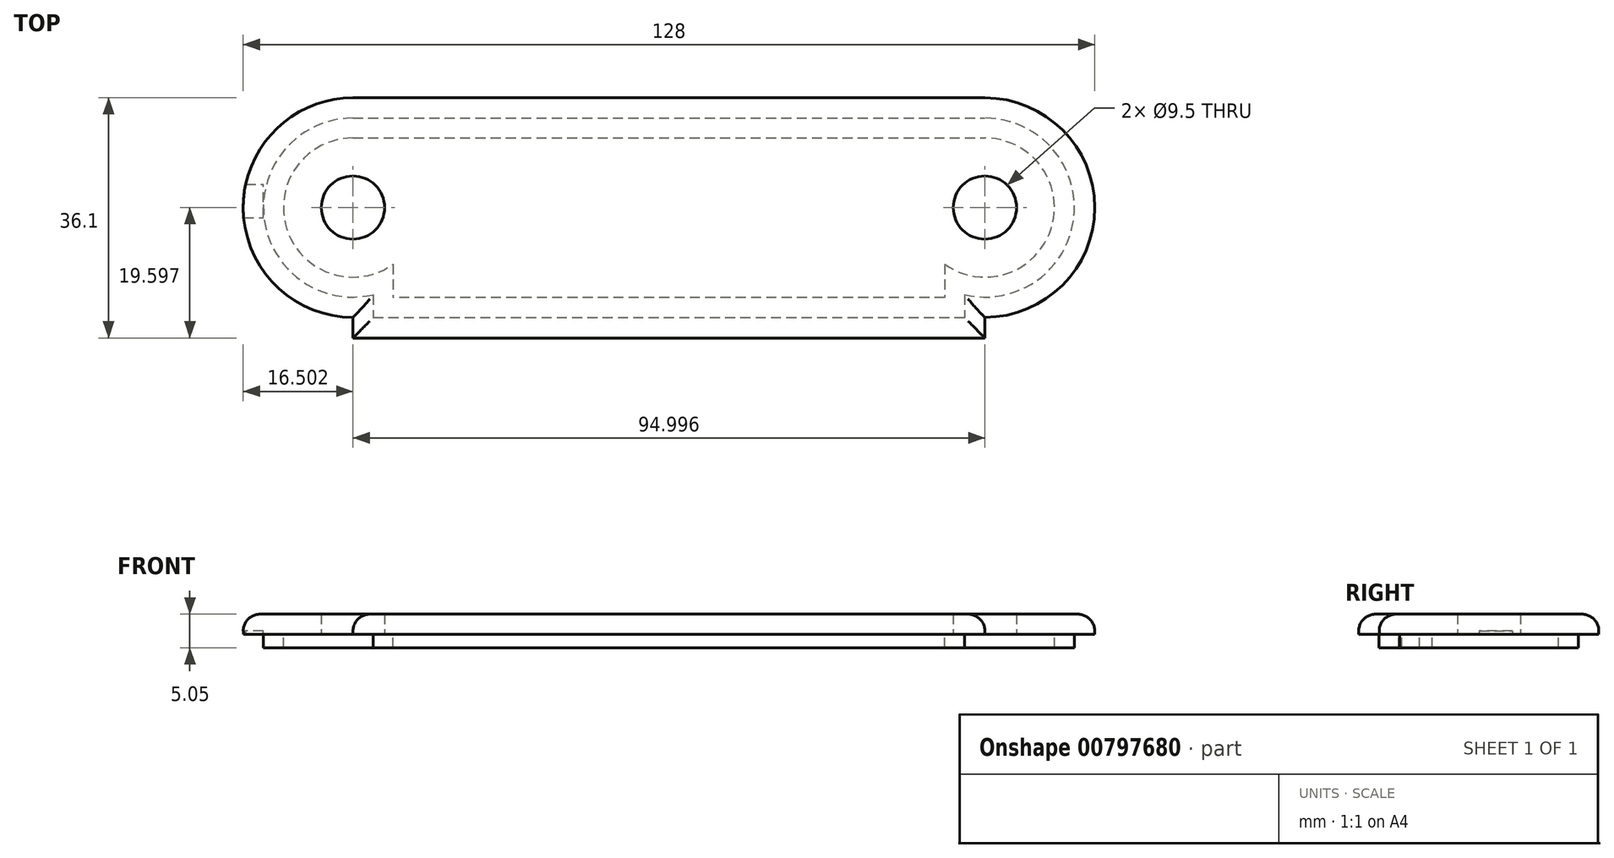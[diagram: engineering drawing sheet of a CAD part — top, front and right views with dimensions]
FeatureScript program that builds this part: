
annotation { "Feature Type Name" : "Feature", "Feature Type Description" : "" }
export const myFeature = defineFeature(function(context is Context, id is Id, definition is map)
    precondition{}
    {
        {
            var Q0;
            Q0=qCreatedBy(makeId("Top.planeOp"),FACE);
            var sketch = newSketch(context, id + "F0", { "sketchPlane" : qUnion([Q0])});
            skLineSegment(sketch, "E0.bottom", {"start": v(47.5, 18.05) * mm, "end": v(-47.5, 18.05) * mm});
            skLineSegment(sketch, "E0.top", {"start": v(47.5, -18.05) * mm, "end": v(-47.5, -18.05) * mm});
            skLineSegment(sketch, "E0.left", {"start": v(47.5, 18.05) * mm, "end": v(47.5, -18.05) * mm});
            skLineSegment(sketch, "E0.right", {"start": v(-47.5, 18.05) * mm, "end": v(-47.5, -18.05) * mm});
            skPoint(sketch, "E0.middle", {"position": v(0, 0) * mm});
            skCircle(sketch, "E1", {"center": v(-47.5, 1.55) * mm, "radius": 16.5 * mm});
            skCircle(sketch, "E2", {"center": v(47.5, 1.55) * mm, "radius": 16.5 * mm});
            skSolve(sketch);
        }
        {
            var Q0;
            Q0=qSketchRegion(id+"F0",true);
            extrude(context, id + "F1", {"entities" : qUnion([Q0]), "depth" : 3.05 * mm, "offsetDistance" : 25.4 * mm});
        }
        {
            var Q0;
            Q0=makeQuery(id+"F1.opExtrude","CAP_EDGE",EDGE,{"disambiguationData":[OSD([sQuery(id+"F0.wireOp",EDGE,"E1")])],"isStart":false});
            var Q1;
            Q1=makeQuery(id+"F1.opExtrude","CAP_EDGE",EDGE,{"disambiguationData":[OSD([sQuery(id+"F0.wireOp",EDGE,"E2")])],"isStart":false});
            var Q2;
            Q2=makeQuery(id+"F1.opExtrude","CAP_FACE",FACE,{"disambiguationData":[OSD([sQuery(id+"F0.wireOp",EDGE,"E0.bottom"),sQuery(id+"F0.wireOp",EDGE,"E0.top"),sQuery(id+"F0.wireOp",EDGE,"E0.left"),sQuery(id+"F0.wireOp",EDGE,"E0.right"),sQuery(id+"F0.wireOp",EDGE,"E1"),sQuery(id+"F0.wireOp",EDGE,"E2")])],"isStart":false});
            fillet(context, id + "F2", {"entities" : qUnion([Q0, Q1, Q2]), "radius" : 2.54 * mm, "tangentPropagation" : true, "allowEdgeOverflow" : false});
        }
        {
            var Q0;
            Q0=qCreatedBy(makeId("Top.planeOp"),FACE);
            var sketch = newSketch(context, id + "F3", { "sketchPlane" : qUnion([Q0])});
            skCircle(sketch, "E3", {"center": v(-47.5, 1.55) * mm, "radius": 4.75 * mm});
            skCircle(sketch, "E4", {"center": v(47.5, 1.55) * mm, "radius": 4.75 * mm});
            skSolve(sketch);
        }
        {
            var Q0;
            Q0=qSketchRegion(id+"F3",true);
            extrude(context, id + "F4", {"entities" : qUnion([Q0]), "operationType" : NewBodyOperationType.REMOVE, "depth" : 3.05 * mm, "offsetDistance" : 25.4 * mm});
        }
        {
            var Q0;
            Q0=qCreatedBy(makeId("Top.planeOp"),FACE);
            var sketch = newSketch(context, id + "F5", { "sketchPlane" : qUnion([Q0])});
            skPoint(sketch, "E5.middle", {"position": v(0, 0) * mm});
            skArc(sketch, "E6.0", {"start": v(44.45, -11.56) * mm, "mid": v(60.86, 0.01) * mm, "end": v(47.5, 15) * mm});
            skArc(sketch, "E6.1", {"start": v(-47.5, 15) * mm, "mid": v(-60.86, 0.01) * mm, "end": v(-44.45, -11.56) * mm});
            skLineSegment(sketch, "E6.2", {"start": v(-44.45, -11.56) * mm, "end": v(-44.45, -15) * mm});
            skLineSegment(sketch, "E6.3", {"start": v(44.45, -15) * mm, "end": v(-44.45, -15) * mm});
            skLineSegment(sketch, "E6.4", {"start": v(44.45, -11.56) * mm, "end": v(44.45, -15) * mm});
            skLineSegment(sketch, "E7", {"start": v(-47.5, 15) * mm, "end": v(47.5, 15) * mm});
            skLineSegment(sketch, "E8.0", {"start": v(41.45, -6.98) * mm, "end": v(41.45, -12) * mm});
            skLineSegment(sketch, "E8.1", {"start": v(-41.45, -6.98) * mm, "end": v(-41.45, -12) * mm});
            skArc(sketch, "E8.2", {"start": v(-47.5, 12) * mm, "mid": v(-57.46, -1.63) * mm, "end": v(-41.45, -6.98) * mm});
            skLineSegment(sketch, "E8.3", {"start": v(41.45, -12) * mm, "end": v(-41.45, -12) * mm});
            skLineSegment(sketch, "E8.4", {"start": v(-47.5, 12) * mm, "end": v(47.5, 12) * mm});
            skArc(sketch, "E8.5", {"start": v(41.45, -6.98) * mm, "mid": v(57.46, -1.63) * mm, "end": v(47.5, 12) * mm});
            skSolve(sketch);
        }
        {
            var Q0;
            Q0=makeQuery(id+"F5.imprint","IMPRINT",FACE,{"disambiguationData":[TD([[makeQuery(id+"F5.imprint","IMPRINT",EDGE,{"derivedFrom":sQuery(id+"F5.wireOp",EDGE,"E6.0")}),1.0]])]});
            extrude(context, id + "F6", {"entities" : qUnion([Q0]), "operationType" : NewBodyOperationType.ADD, "oppositeDirection" : true, "depth" : 2 * mm, "offsetDistance" : 25.4 * mm});
        }
        {
            var Q0;
            Q0=qCreatedBy(makeId("Right.planeOp"),FACE);
            cPlane(context, id + "F7", {"entities" : qUnion([Q0]), "cplaneType" : CPlaneType.OFFSET, "offset" : 65 * mm, "oppositeDirection" : true, "width" : 152.4 * mm, "height" : 152.4 * mm});
        }
        {
            var Q0;
            Q0=qCreatedBy(id+"F7.planeOp",FACE);
            var sketch = newSketch(context, id + "F8", { "sketchPlane" : qUnion([Q0])});
            skLineSegment(sketch, "E9.bottom", {"start": v(0.05, -0.5) * mm, "end": v(5.05, -0.5) * mm});
            skLineSegment(sketch, "E9.top", {"start": v(0.05, 0.5) * mm, "end": v(5.05, 0.5) * mm});
            skLineSegment(sketch, "E9.left", {"start": v(0.05, -0.5) * mm, "end": v(0.05, 0.5) * mm});
            skLineSegment(sketch, "E9.right", {"start": v(5.05, -0.5) * mm, "end": v(5.05, 0.5) * mm});
            skPoint(sketch, "E9.middle", {"position": v(2.55, 0) * mm});
            skSolve(sketch);
        }
        {
            var Q0;
            Q0=qSketchRegion(id+"F8",true);
            extrude(context, id + "F9", {"entities" : qUnion([Q0]), "operationType" : NewBodyOperationType.REMOVE, "depth" : 4 * mm, "offsetDistance" : 25.4 * mm});
        }
    });
